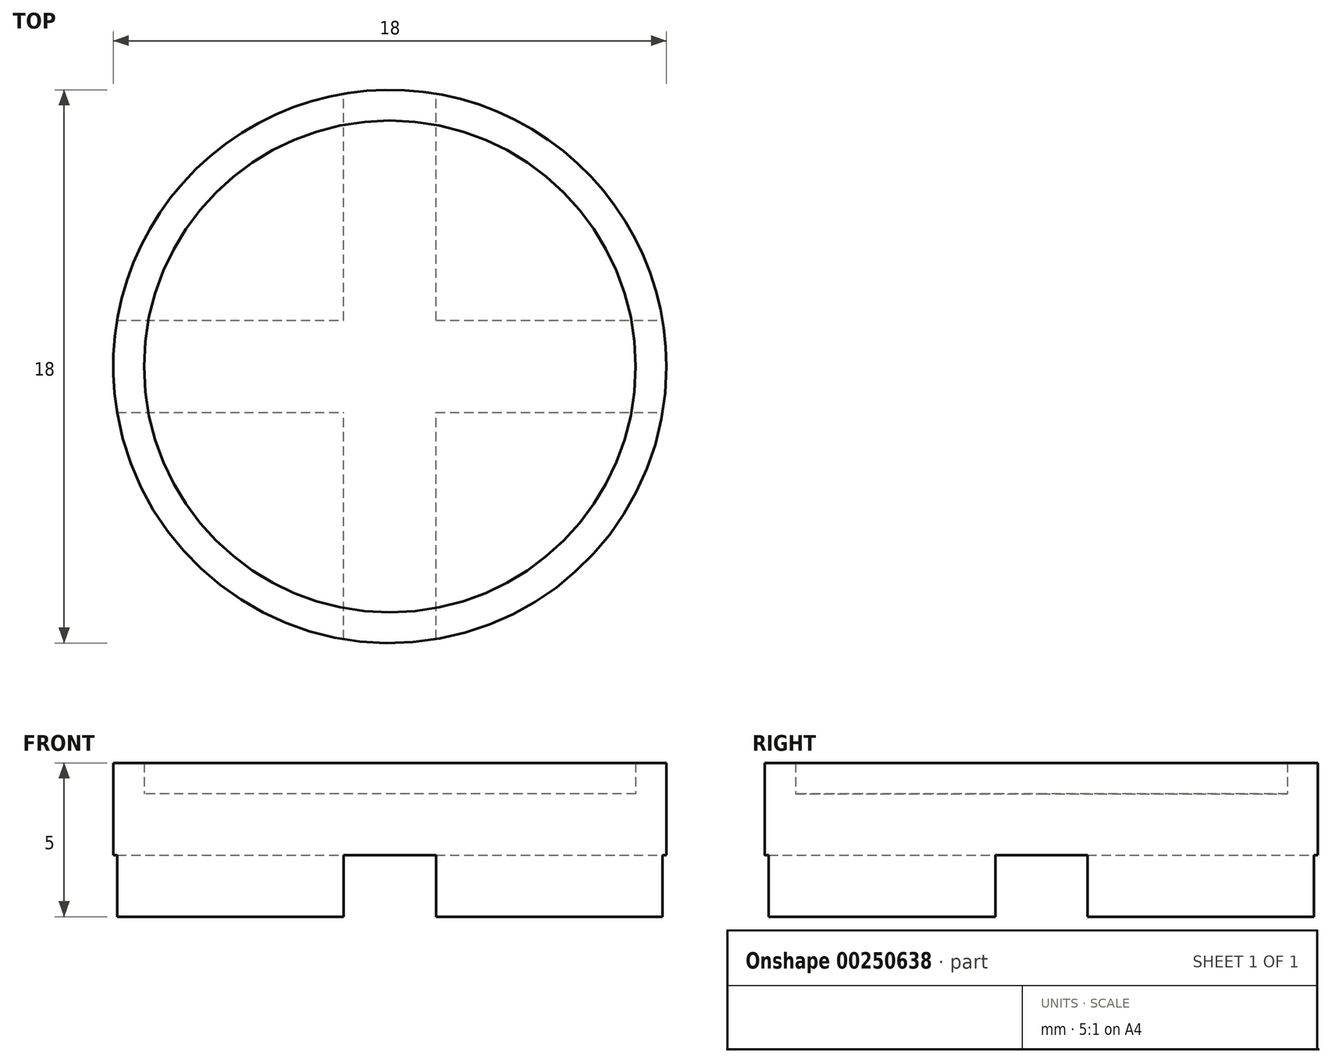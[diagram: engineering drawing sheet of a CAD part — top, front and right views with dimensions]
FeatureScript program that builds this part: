
annotation { "Feature Type Name" : "Feature", "Feature Type Description" : "" }
export const myFeature = defineFeature(function(context is Context, id is Id, definition is map)
    precondition{}
    {
        {
            var Q0;
            Q0=qCreatedBy(makeId("Top.planeOp"),FACE);
            var sketch = newSketch(context, id + "F0", { "sketchPlane" : qUnion([Q0])});
            skCircle(sketch, "E0", {"center": v(-31.33, 19.76) * mm, "radius": 9 * mm});
            skSolve(sketch);
        }
        {
            var Q0;
            Q0=qSketchRegion(id+"F0",true);
            extrude(context, id + "F1", {"entities" : qUnion([Q0]), "depth" : 4 * mm});
        }
        {
            var Q0;
            Q0=makeQuery(id+"F1.opExtrude","CAP_FACE",FACE,{"disambiguationData":[OSD([sQuery(id+"F0.wireOp",EDGE,"E0")])],"isStart":false});
            var sketch = newSketch(context, id + "F2", { "sketchPlane" : qUnion([Q0])});
            skCircle(sketch, "E1", {"center": v(-31.33, 19.76) * mm, "radius": 8 * mm});
            skCircle(sketch, "E2", {"center": v(-31.33, 19.76) * mm, "radius": 9 * mm});
            skSolve(sketch);
        }
        {
            var Q0;
            Q0=makeQuery(id+"F1.opExtrude","CAP_FACE",FACE,{"disambiguationData":[OSD([sQuery(id+"F0.wireOp",EDGE,"E0")])],"isStart":true});
            var sketch = newSketch(context, id + "F3", { "sketchPlane" : qUnion([Q0])});
            skLineSegment(sketch, "E3", {"start": v(-31.33, -19.76) * mm, "end": v(-22.33, -19.76) * mm, "construction": true});
            skLineSegment(sketch, "E4", {"start": v(-31.33, -19.76) * mm, "end": v(-31.33, -10.76) * mm, "construction": true});
            skLineSegment(sketch, "E5", {"start": v(-31.33, -19.76) * mm, "end": v(-40.33, -19.76) * mm, "construction": true});
            skLineSegment(sketch, "E6", {"start": v(-31.33, -19.76) * mm, "end": v(-31.33, -28.76) * mm, "construction": true});
            skLineSegment(sketch, "E7.bottom", {"start": v(-40.33, -28.76) * mm, "end": v(-22.33, -28.76) * mm});
            skLineSegment(sketch, "E7.top", {"start": v(-40.33, -10.76) * mm, "end": v(-22.33, -10.76) * mm});
            skLineSegment(sketch, "E7.left", {"start": v(-22.33, -10.76) * mm, "end": v(-22.33, -28.76) * mm});
            skLineSegment(sketch, "E7.right", {"start": v(-40.33, -10.76) * mm, "end": v(-40.33, -28.76) * mm});
            skPoint(sketch, "E8", {"position": v(-31.33, -28.76) * mm});
            skPoint(sketch, "E9", {"position": v(-40.33, -19.76) * mm});
            skPoint(sketch, "E10", {"position": v(-22.33, -19.76) * mm});
            skPoint(sketch, "E11", {"position": v(-31.33, -10.76) * mm});
            skLineSegment(sketch, "E12.bottom", {"start": v(-32.83, -10.76) * mm, "end": v(-29.83, -10.76) * mm});
            skLineSegment(sketch, "E12.top", {"start": v(-32.83, -28.76) * mm, "end": v(-29.83, -28.76) * mm});
            skLineSegment(sketch, "E12.left", {"start": v(-32.83, -10.76) * mm, "end": v(-32.83, -28.76) * mm});
            skLineSegment(sketch, "E12.right", {"start": v(-29.83, -10.76) * mm, "end": v(-29.83, -28.76) * mm});
            skLineSegment(sketch, "E13.bottom", {"start": v(-40.33, -18.26) * mm, "end": v(-22.33, -18.26) * mm});
            skLineSegment(sketch, "E13.top", {"start": v(-40.33, -21.26) * mm, "end": v(-22.33, -21.26) * mm});
            skLineSegment(sketch, "E13.left", {"start": v(-40.33, -18.26) * mm, "end": v(-40.33, -21.26) * mm});
            skLineSegment(sketch, "E13.right", {"start": v(-22.33, -18.26) * mm, "end": v(-22.33, -21.26) * mm});
            skSolve(sketch);
        }
        {
            var Q0;
            {var subQ1=sQuery(id+"F3.wireOp",EDGE,"E12.bottom");var subQ3=makeQuery(id+"F1.opExtrude","CAP_EDGE",EDGE,{"disambiguationData":[OSD([sQuery(id+"F0.wireOp",EDGE,"E0")])],"isStart":true});var subQ4=makeQuery(id+"F3.imprint","INTERSECT",VERTEX,{"derivedFrom":[subQ3,subQ1]});Q0=makeQuery(id+"F3.imprint","IMPRINT",FACE,{"disambiguationData":[TD([[makeQuery(id+"F3.imprint","IMPRINT",EDGE,{"disambiguationData":[TD([[subQ4,1.0]])],"derivedFrom":subQ3}),1.0]])]});}
            var Q1;
            {var subQ1=sQuery(id+"F3.wireOp",EDGE,"E12.bottom");var subQ3=makeQuery(id+"F1.opExtrude","CAP_EDGE",EDGE,{"disambiguationData":[OSD([sQuery(id+"F0.wireOp",EDGE,"E0")])],"isStart":true});var subQ4=makeQuery(id+"F3.imprint","INTERSECT",VERTEX,{"derivedFrom":[subQ3,subQ1]});Q1=makeQuery(id+"F3.imprint","IMPRINT",FACE,{"disambiguationData":[TD([[makeQuery(id+"F3.imprint","IMPRINT",EDGE,{"disambiguationData":[TD([[subQ4,-1.0]])],"derivedFrom":subQ3}),1.0]])]});}
            var Q2;
            {var subQ1=sQuery(id+"F3.wireOp",EDGE,"E12.top");var subQ3=makeQuery(id+"F1.opExtrude","CAP_EDGE",EDGE,{"disambiguationData":[OSD([sQuery(id+"F0.wireOp",EDGE,"E0")])],"isStart":true});var subQ4=makeQuery(id+"F3.imprint","INTERSECT",VERTEX,{"derivedFrom":[subQ3,subQ1]});Q2=makeQuery(id+"F3.imprint","IMPRINT",FACE,{"disambiguationData":[TD([[makeQuery(id+"F3.imprint","IMPRINT",EDGE,{"disambiguationData":[TD([[subQ4,-1.0]])],"derivedFrom":subQ3}),1.0]])]});}
            var Q3;
            {var subQ1=sQuery(id+"F3.wireOp",EDGE,"E12.top");var subQ3=makeQuery(id+"F1.opExtrude","CAP_EDGE",EDGE,{"disambiguationData":[OSD([sQuery(id+"F0.wireOp",EDGE,"E0")])],"isStart":true});var subQ4=makeQuery(id+"F3.imprint","INTERSECT",VERTEX,{"derivedFrom":[subQ3,subQ1]});Q3=makeQuery(id+"F3.imprint","IMPRINT",FACE,{"disambiguationData":[TD([[makeQuery(id+"F3.imprint","IMPRINT",EDGE,{"disambiguationData":[TD([[subQ4,1.0]])],"derivedFrom":subQ3}),1.0]])]});}
            var Q4;
            {var subQ0=sQuery(id+"F3.wireOp",EDGE,"E13.left");var subQ3=makeQuery(id+"F1.opExtrude","CAP_EDGE",EDGE,{"disambiguationData":[OSD([sQuery(id+"F0.wireOp",EDGE,"E0")])],"isStart":true});var subQ5=makeQuery(id+"F3.imprint","INTERSECT",VERTEX,{"derivedFrom":[subQ3,subQ0]});Q4=makeQuery(id+"F3.imprint","IMPRINT",FACE,{"disambiguationData":[TD([[makeQuery(id+"F3.imprint","IMPRINT",EDGE,{"disambiguationData":[TD([[subQ5,-1.0]])],"derivedFrom":subQ3}),1.0]])]});}
            var Q5;
            {var subQ0=sQuery(id+"F3.wireOp",EDGE,"E13.right");var subQ3=makeQuery(id+"F1.opExtrude","CAP_EDGE",EDGE,{"disambiguationData":[OSD([sQuery(id+"F0.wireOp",EDGE,"E0")])],"isStart":true});var subQ5=makeQuery(id+"F3.imprint","INTERSECT",VERTEX,{"derivedFrom":[subQ3,subQ0]});Q5=makeQuery(id+"F3.imprint","IMPRINT",FACE,{"disambiguationData":[TD([[makeQuery(id+"F3.imprint","IMPRINT",EDGE,{"disambiguationData":[TD([[subQ5,1.0]])],"derivedFrom":subQ3}),1.0]])]});}
            var Q6;
            {var subQ0=sQuery(id+"F3.wireOp",EDGE,"E13.left");var subQ3=makeQuery(id+"F1.opExtrude","CAP_EDGE",EDGE,{"disambiguationData":[OSD([sQuery(id+"F0.wireOp",EDGE,"E0")])],"isStart":true});var subQ5=makeQuery(id+"F3.imprint","INTERSECT",VERTEX,{"derivedFrom":[subQ3,subQ0]});Q6=makeQuery(id+"F3.imprint","IMPRINT",FACE,{"disambiguationData":[TD([[makeQuery(id+"F3.imprint","IMPRINT",EDGE,{"disambiguationData":[TD([[subQ5,1.0]])],"derivedFrom":subQ3}),1.0]])]});}
            var Q7;
            {var subQ0=sQuery(id+"F3.wireOp",EDGE,"E13.right");var subQ3=makeQuery(id+"F1.opExtrude","CAP_EDGE",EDGE,{"disambiguationData":[OSD([sQuery(id+"F0.wireOp",EDGE,"E0")])],"isStart":true});var subQ5=makeQuery(id+"F3.imprint","INTERSECT",VERTEX,{"derivedFrom":[subQ3,subQ0]});Q7=makeQuery(id+"F3.imprint","IMPRINT",FACE,{"disambiguationData":[TD([[makeQuery(id+"F3.imprint","IMPRINT",EDGE,{"disambiguationData":[TD([[subQ5,-1.0]])],"derivedFrom":subQ3}),1.0]])]});}
            var Q8;
            {var subQ3=makeQuery(id+"F1.opExtrude","CAP_EDGE",EDGE,{"disambiguationData":[OSD([sQuery(id+"F0.wireOp",EDGE,"E0")])],"isStart":true});var subQ5=sQuery(id+"F3.wireOp",EDGE,"E12.left");var subQ8=makeQuery(id+"F3.imprint","INTERSECT",VERTEX,{"disambiguationData":[OD(1.0)],"derivedFrom":[subQ3,subQ5]});Q8=makeQuery(id+"F3.imprint","IMPRINT",FACE,{"disambiguationData":[TD([[makeQuery(id+"F3.imprint","IMPRINT",EDGE,{"disambiguationData":[TD([[subQ8,-1.0]])],"derivedFrom":subQ3}),1.0]])]});}
            var Q9;
            {var subQ3=makeQuery(id+"F1.opExtrude","CAP_EDGE",EDGE,{"disambiguationData":[OSD([sQuery(id+"F0.wireOp",EDGE,"E0")])],"isStart":true});var subQ5=sQuery(id+"F3.wireOp",EDGE,"E12.right");var subQ8=makeQuery(id+"F3.imprint","INTERSECT",VERTEX,{"disambiguationData":[OD(1.0)],"derivedFrom":[subQ3,subQ5]});Q9=makeQuery(id+"F3.imprint","IMPRINT",FACE,{"disambiguationData":[TD([[makeQuery(id+"F3.imprint","IMPRINT",EDGE,{"disambiguationData":[TD([[subQ8,1.0]])],"derivedFrom":subQ3}),1.0]])]});}
            var Q10;
            {var subQ3=makeQuery(id+"F1.opExtrude","CAP_EDGE",EDGE,{"disambiguationData":[OSD([sQuery(id+"F0.wireOp",EDGE,"E0")])],"isStart":true});var subQ5=sQuery(id+"F3.wireOp",EDGE,"E12.left");var subQ8=makeQuery(id+"F3.imprint","INTERSECT",VERTEX,{"disambiguationData":[OD(0.0)],"derivedFrom":[subQ3,subQ5]});Q10=makeQuery(id+"F3.imprint","IMPRINT",FACE,{"disambiguationData":[TD([[makeQuery(id+"F3.imprint","IMPRINT",EDGE,{"disambiguationData":[TD([[subQ8,1.0]])],"derivedFrom":subQ3}),1.0]])]});}
            var Q11;
            {var subQ3=makeQuery(id+"F1.opExtrude","CAP_EDGE",EDGE,{"disambiguationData":[OSD([sQuery(id+"F0.wireOp",EDGE,"E0")])],"isStart":true});var subQ5=sQuery(id+"F3.wireOp",EDGE,"E12.right");var subQ8=makeQuery(id+"F3.imprint","INTERSECT",VERTEX,{"disambiguationData":[OD(0.0)],"derivedFrom":[subQ3,subQ5]});Q11=makeQuery(id+"F3.imprint","IMPRINT",FACE,{"disambiguationData":[TD([[makeQuery(id+"F3.imprint","IMPRINT",EDGE,{"disambiguationData":[TD([[subQ8,-1.0]])],"derivedFrom":subQ3}),1.0]])]});}
            var Q12;
            {var subQ2=sQuery(id+"F3.wireOp",EDGE,"E12.left");var subQ4=sQuery(id+"F3.wireOp",EDGE,"E13.bottom");var subQ8=makeQuery(id+"F3.imprint","INTERSECT",VERTEX,{"derivedFrom":[subQ2,subQ4]});Q12=makeQuery(id+"F3.imprint","IMPRINT",FACE,{"disambiguationData":[TD([[makeQuery(id+"F3.imprint","IMPRINT",EDGE,{"disambiguationData":[TD([[subQ8,1.0]])],"derivedFrom":subQ2}),1.0]])]});}
            var Q13;
            {var subQ1=sQuery(id+"F3.wireOp",EDGE,"E12.left");var subQ5=sQuery(id+"F3.wireOp",EDGE,"E13.bottom");var subQ6=makeQuery(id+"F3.imprint","INTERSECT",VERTEX,{"derivedFrom":[subQ1,subQ5]});Q13=makeQuery(id+"F3.imprint","IMPRINT",FACE,{"disambiguationData":[TD([[makeQuery(id+"F3.imprint","IMPRINT",EDGE,{"disambiguationData":[TD([[subQ6,-1.0]])],"derivedFrom":subQ1}),-1.0]])]});}
            var Q14;
            {var subQ0=sQuery(id+"F3.wireOp",EDGE,"E13.top");var subQ1=sQuery(id+"F3.wireOp",EDGE,"E12.left");var subQ2=makeQuery(id+"F3.imprint","INTERSECT",VERTEX,{"derivedFrom":[subQ1,subQ0]});Q14=makeQuery(id+"F3.imprint","IMPRINT",FACE,{"disambiguationData":[TD([[makeQuery(id+"F3.imprint","IMPRINT",EDGE,{"disambiguationData":[TD([[subQ2,-1.0]])],"derivedFrom":subQ1}),1.0]])]});}
            var Q15;
            {var subQ2=sQuery(id+"F3.wireOp",EDGE,"E13.bottom");var subQ5=sQuery(id+"F3.wireOp",EDGE,"E12.right");var subQ8=makeQuery(id+"F3.imprint","INTERSECT",VERTEX,{"derivedFrom":[subQ5,subQ2]});Q15=makeQuery(id+"F3.imprint","IMPRINT",FACE,{"disambiguationData":[TD([[makeQuery(id+"F3.imprint","IMPRINT",EDGE,{"disambiguationData":[TD([[subQ8,-1.0]])],"derivedFrom":subQ5}),1.0]])]});}
            var Q16;
            {var subQ0=sQuery(id+"F3.wireOp",EDGE,"E13.bottom");var subQ1=sQuery(id+"F3.wireOp",EDGE,"E12.left");var subQ2=makeQuery(id+"F3.imprint","INTERSECT",VERTEX,{"derivedFrom":[subQ1,subQ0]});Q16=makeQuery(id+"F3.imprint","IMPRINT",FACE,{"disambiguationData":[TD([[makeQuery(id+"F3.imprint","IMPRINT",EDGE,{"disambiguationData":[TD([[subQ2,-1.0]])],"derivedFrom":subQ1}),1.0]])]});}
            extrude(context, id + "F4", {"entities" : qUnion([Q0, Q1, Q2, Q3, Q4, Q5, Q6, Q7, Q8, Q9, Q10, Q11, Q12, Q13, Q14, Q15, Q16]), "operationType" : NewBodyOperationType.REMOVE, "oppositeDirection" : true, "depth" : 2 * mm});
        }
        {
            var Q0;
            Q0=qSketchRegion(id+"F2",true);
            var Q1;
            Q1=makeQuery(id+"F2.imprint","IMPRINT",FACE,{"disambiguationData":[TD([[makeQuery(id+"F2.imprint","IMPRINT",EDGE,{"derivedFrom":sQuery(id+"F2.wireOp",EDGE,"hKqnuJLd-dfdz-vJIs-yDKo-c4hLNRw30SuP")}),-1.0]])]});
            extrude(context, id + "F5", {"entities" : qUnion([Q0, Q1]), "operationType" : NewBodyOperationType.ADD, "depth" : 1 * mm});
        }
    });
